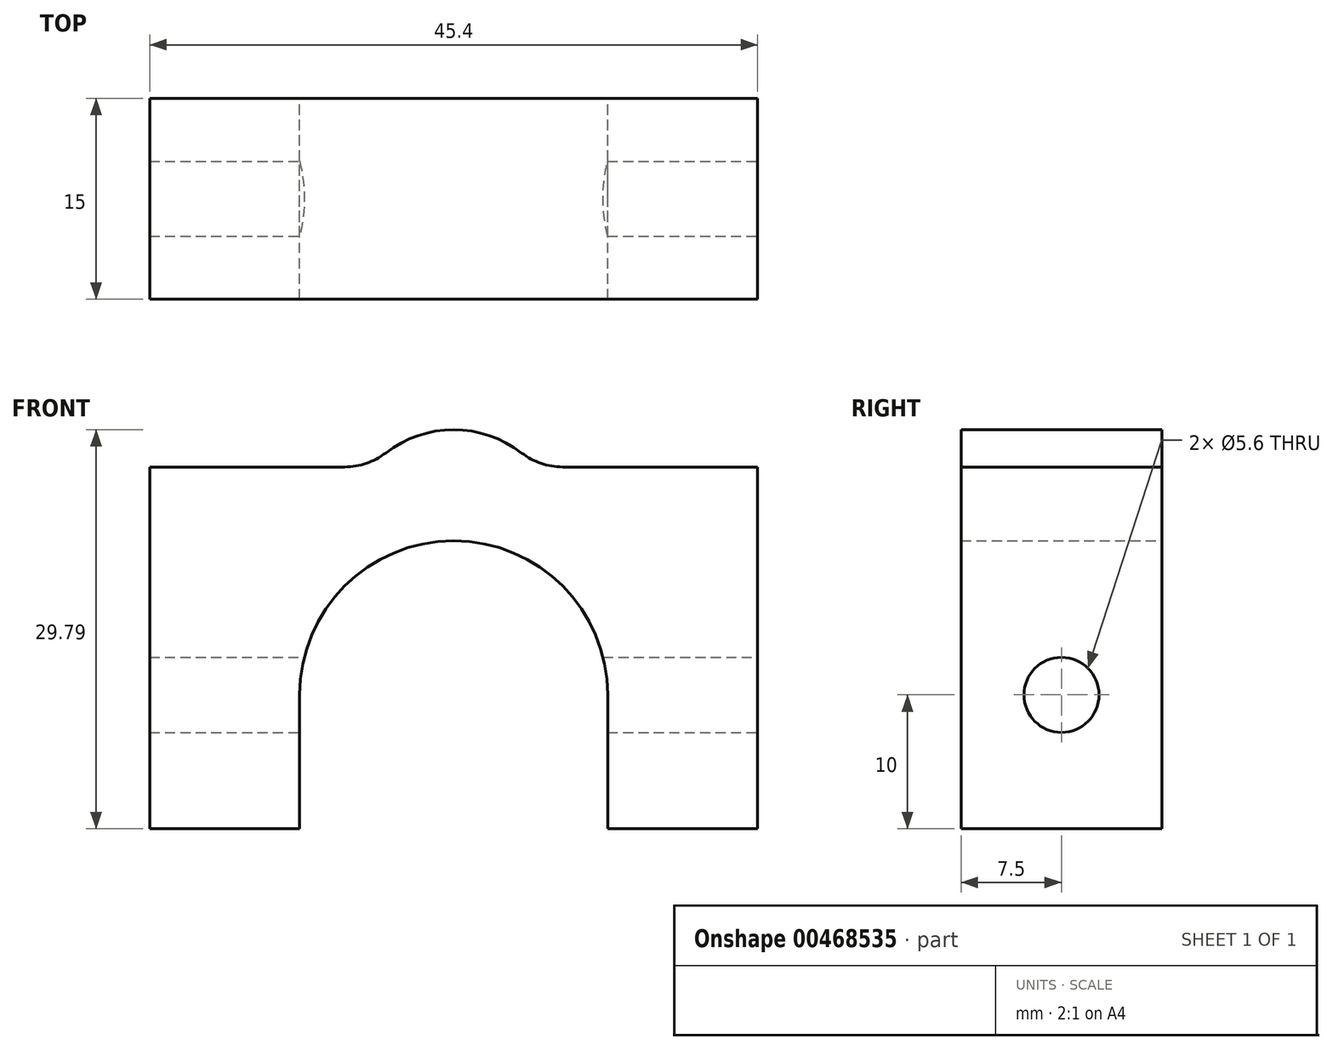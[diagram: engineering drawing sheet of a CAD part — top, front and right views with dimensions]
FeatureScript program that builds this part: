
annotation { "Feature Type Name" : "Feature", "Feature Type Description" : "" }
export const myFeature = defineFeature(function(context is Context, id is Id, definition is map)
    precondition{}
    {
        {
            var Q0;
            Q0=qCreatedBy(makeId("Front.planeOp"),FACE);
            var sketch = newSketch(context, id + "F0", { "sketchPlane" : qUnion([Q0])});
            skArc(sketch, "E0", {"start": v(11.5, 0) * mm, "mid": v(0, 11.5) * mm, "end": v(-11.5, 0) * mm});
            skLineSegment(sketch, "E1.top", {"start": v(-22.7, 17.01) * mm, "end": v(-6.2, 17.01) * mm});
            skLineSegment(sketch, "E1.left", {"start": v(-22.7, 0) * mm, "end": v(-22.7, 17.01) * mm});
            skLineSegment(sketch, "E1.right", {"start": v(22.7, 0) * mm, "end": v(22.7, 17.01) * mm});
            skArc(sketch, "E2", {"start": v(6.2, 17.01) * mm, "mid": v(0, 19.8) * mm, "end": v(-6.2, 17.01) * mm});
            skLineSegment(sketch, "E3.trimOffspring", {"start": v(6.2, 17.01) * mm, "end": v(22.7, 17.01) * mm});
            skLineSegment(sketch, "E4.top", {"start": v(-22.7, -10) * mm, "end": v(-11.5, -10) * mm});
            skLineSegment(sketch, "E4.left", {"start": v(-22.7, 0) * mm, "end": v(-22.7, -10) * mm});
            skLineSegment(sketch, "E4.right", {"start": v(-11.5, 0) * mm, "end": v(-11.5, -10) * mm});
            skLineSegment(sketch, "E5.top", {"start": v(11.5, -10) * mm, "end": v(22.7, -10) * mm});
            skLineSegment(sketch, "E5.left", {"start": v(11.5, 0) * mm, "end": v(11.5, -10) * mm});
            skLineSegment(sketch, "E5.right", {"start": v(22.7, 0) * mm, "end": v(22.7, -10) * mm});
            skSolve(sketch);
        }
        {
            var Q0;
            Q0=makeQuery(id+"F0.imprint","IMPRINT",FACE,{"disambiguationData":[TD([[makeQuery(id+"F0.imprint","IMPRINT",EDGE,{"derivedFrom":sQuery(id+"F0.wireOp",EDGE,"E0")}),-1.0]])]});
            extrude(context, id + "F1", {"entities" : qUnion([Q0]), "depth" : 15 * mm, "offsetDistance" : 25 * mm});
        }
        {
            var Q0;
            Q0=makeQuery(id+"F1.opExtrude","SWEPT_FACE",FACE,{"disambiguationData":[OSD([sQuery(id+"F0.wireOp",EDGE,"E1.right"),sQuery(id+"F0.wireOp",EDGE,"E5.right")])]});
            var sketch = newSketch(context, id + "F2", { "sketchPlane" : qUnion([Q0])});
            skLineSegment(sketch, "E6", {"start": v(-15, 0) * mm, "end": v(0, 0) * mm, "construction": true});
            skPoint(sketch, "E7", {"position": v(-7.5, 0) * mm});
            skCircle(sketch, "E8", {"center": v(-7.5, 0) * mm, "radius": 2.8 * mm});
            skSolve(sketch);
        }
        {
            var Q0;
            Q0=makeQuery(id+"F2.imprint","IMPRINT",FACE,{"disambiguationData":[TD([[makeQuery(id+"F2.imprint","IMPRINT",EDGE,{"derivedFrom":sQuery(id+"F2.wireOp",EDGE,"E8")}),1.0]])]});
            extrude(context, id + "F3", {"entities" : qUnion([Q0]), "operationType" : NewBodyOperationType.REMOVE, "endBound" : BoundingType.THROUGH_ALL, "oppositeDirection" : true, "depth" : 25 * mm, "offsetDistance" : 25 * mm});
        }
        {
            var Q0;
            Q0=makeQuery(id+"F1.opExtrude","SWEPT_EDGE",EDGE,{"disambiguationData":[OSD([sQuery(id+"F0.wireOp",EDGE,"E2"),sQuery(id+"F0.wireOp",EDGE,"E3.trimOffspring")])]});
            var Q1;
            Q1=makeQuery(id+"F1.opExtrude","SWEPT_EDGE",EDGE,{"disambiguationData":[OSD([sQuery(id+"F0.wireOp",EDGE,"E1.top"),sQuery(id+"F0.wireOp",EDGE,"E2")])]});
            fillet(context, id + "F4", {"entities" : qUnion([Q0, Q1]), "radius" : 5 * mm, "tangentPropagation" : true, "allowEdgeOverflow" : false});
        }
    });
